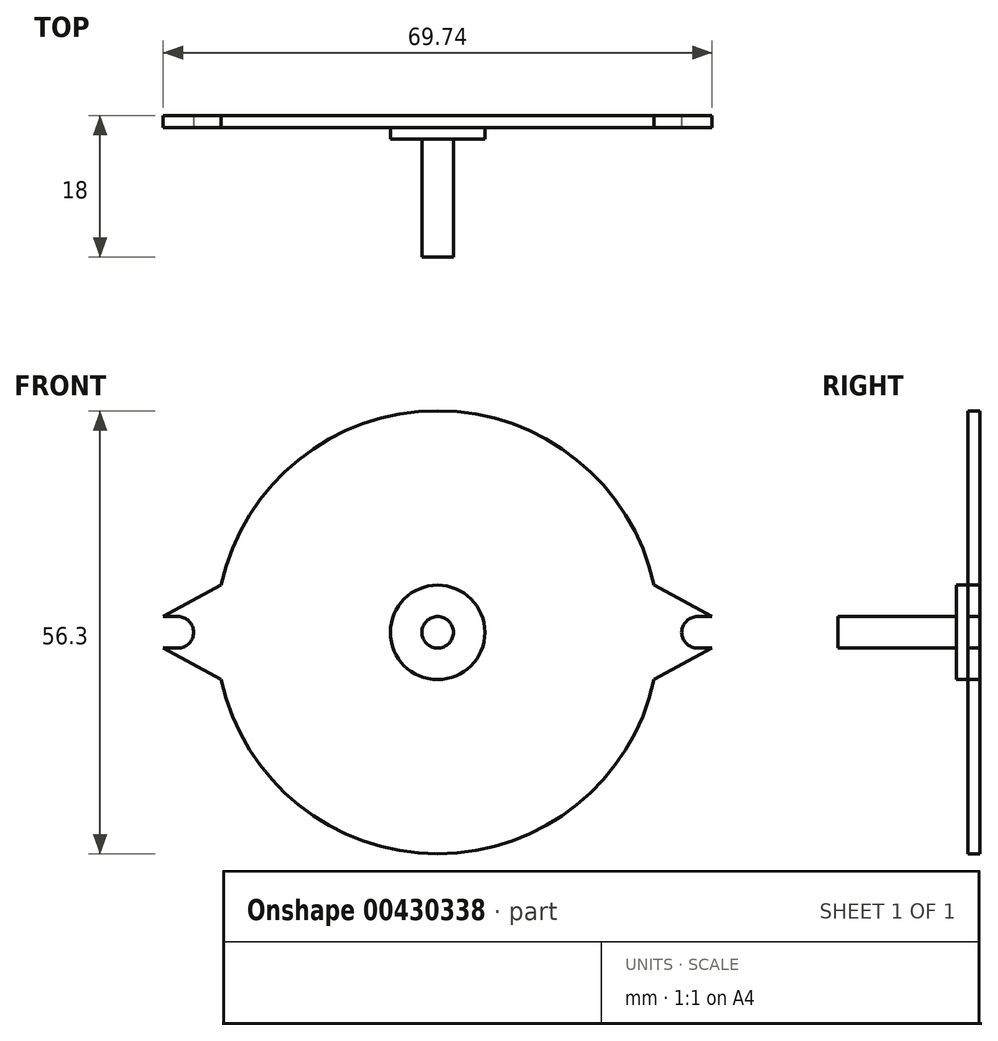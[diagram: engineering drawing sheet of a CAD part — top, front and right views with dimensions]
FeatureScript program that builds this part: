
annotation { "Feature Type Name" : "Feature", "Feature Type Description" : "" }
export const myFeature = defineFeature(function(context is Context, id is Id, definition is map)
    precondition{}
    {
        {
            var Q0;
            Q0=qCreatedBy(makeId("Front.planeOp"),FACE);
            var sketch = newSketch(context, id + "F0", { "sketchPlane" : qUnion([Q0])});
            skCircle(sketch, "E0", {"center": v(0, 0) * mm, "radius": 28.15 * mm});
            skLineSegment(sketch, "E1", {"start": v(0, 0) * mm, "end": v(33, 0) * mm});
            skLineSegment(sketch, "E2.MirrorCS", {"start": v(0, 0) * mm, "end": v(-33, 0) * mm});
            skLineSegment(sketch, "E3.0", {"start": v(34.87, 2) * mm, "end": v(33, 2) * mm});
            skLineSegment(sketch, "E4.0", {"start": v(34.87, -2) * mm, "end": v(33, -2) * mm});
            skArc(sketch, "E5", {"start": v(33, 2) * mm, "mid": v(31, 0) * mm, "end": v(33, -2) * mm});
            skLineSegment(sketch, "E6", {"start": v(34.87, 2) * mm, "end": v(27.5, 6) * mm});
            skLineSegment(sketch, "E7.MirrorCS", {"start": v(34.87, -2) * mm, "end": v(27.5, -6) * mm});
            skLineSegment(sketch, "E8.MirrorCS", {"start": v(-34.87, -2) * mm, "end": v(-33, -2) * mm});
            skLineSegment(sketch, "E9.MirrorCS", {"start": v(-34.87, 2) * mm, "end": v(-33, 2) * mm});
            skLineSegment(sketch, "E10.MirrorCS", {"start": v(-34.87, -2) * mm, "end": v(-27.5, -6) * mm});
            skLineSegment(sketch, "E11.MirrorCS", {"start": v(-34.87, 2) * mm, "end": v(-27.5, 6) * mm});
            skArc(sketch, "E12.MirrorCS", {"start": v(-33, 2) * mm, "mid": v(-31, 0) * mm, "end": v(-33, -2) * mm});
            skSolve(sketch);
        }
        {
            var Q0;
            {var subQ3=sQuery(id+"F0.wireOp",EDGE,"E0");var subQ6=makeQuery(id+"F0.imprint","INTERSECT",VERTEX,{"derivedFrom":[subQ3,sQuery(id+"F0.wireOp",EDGE,"0b0c5fe9-ff03-4a5e-8776-be8f2646c23f0.MirrorCS")]});Q0=makeQuery(id+"F0.imprint","IMPRINT",FACE,{"disambiguationData":[TD([[makeQuery(id+"F0.imprint","IMPRINT",EDGE,{"disambiguationData":[TD([[subQ6,1.0]])],"derivedFrom":subQ3}),1.0]])]});}
            var sketch = newSketch(context, id + "F1", { "sketchPlane" : qUnion([Q0])});
            skCircle(sketch, "E13", {"center": v(0, 0) * mm, "radius": 6 * mm});
            skSolve(sketch);
        }
        {
            var Q0;
            Q0 = qSketchRegion(id + "F1", true);
            extrude(context, id + "F2", {"entities" : qUnion([Q0]), "depth" : 1.5 * mm});
        }
        {
            var Q0;
            Q0=makeQuery(id+"F2.opExtrude","CAP_FACE",FACE,{"disambiguationData":[OSD([sQuery(id+"F1.wireOp",EDGE,"E13")])],"isStart":false});
            var sketch = newSketch(context, id + "F3", { "sketchPlane" : qUnion([Q0])});
            skCircle(sketch, "E14", {"center": v(0, 0) * mm, "radius": 2 * mm});
            skSolve(sketch);
        }
        {
            var Q0;
            Q0 = qSketchRegion(id + "F3", true);
            extrude(context, id + "F4", {"entities" : qUnion([Q0]), "operationType" : NewBodyOperationType.ADD, "depth" : 15 * mm});
        }
        {
            var Q0;
            Q0 = qSketchRegion(id + "F0", true);
            extrude(context, id + "F5", {"entities" : qUnion([Q0]), "operationType" : NewBodyOperationType.ADD, "depth" : -1.5 * mm});
        }
    });
